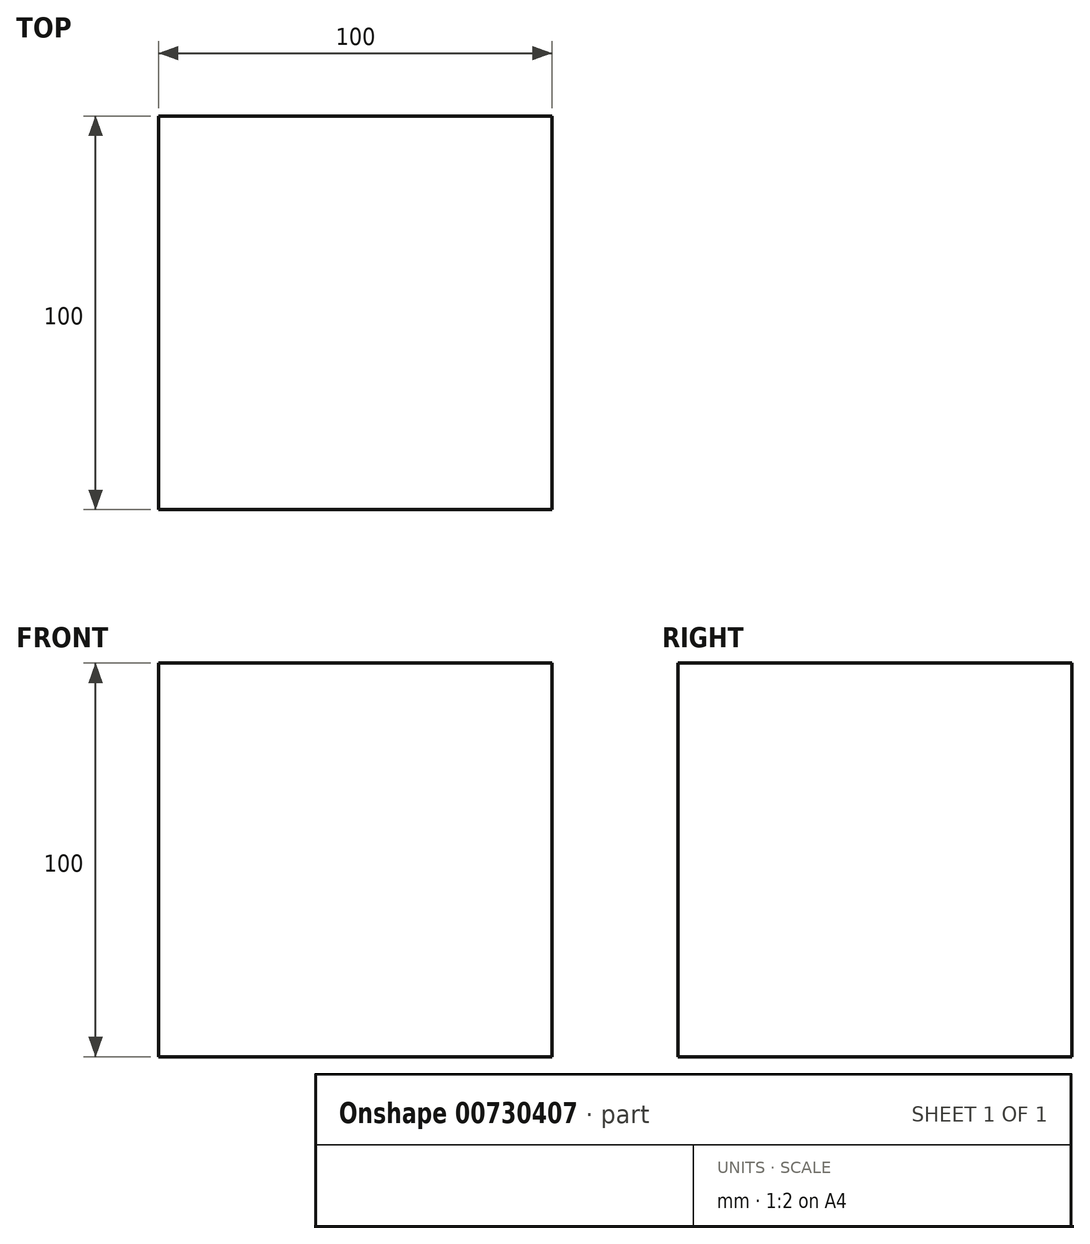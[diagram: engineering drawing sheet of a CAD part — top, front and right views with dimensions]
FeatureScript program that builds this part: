
annotation { "Feature Type Name" : "Feature", "Feature Type Description" : "" }
export const myFeature = defineFeature(function(context is Context, id is Id, definition is map)
    precondition{}
    {
        {
            var Q0;
            Q0=qCreatedBy(makeId("Front.planeOp"),FACE);
            var sketch = newSketch(context, id + "F0", { "sketchPlane" : qUnion([Q0])});
            skLineSegment(sketch, "E0.bottom", {"start": v(50, -50) * mm, "end": v(-50, -50) * mm});
            skLineSegment(sketch, "E0.top", {"start": v(50, 50) * mm, "end": v(-50, 50) * mm});
            skLineSegment(sketch, "E0.left", {"start": v(50, -50) * mm, "end": v(50, 50) * mm});
            skLineSegment(sketch, "E0.right", {"start": v(-50, -50) * mm, "end": v(-50, 50) * mm});
            skPoint(sketch, "E0.middle", {"position": v(0, 0) * mm});
            skSolve(sketch);
        }
        {
            var Q0;
            Q0=makeQuery(id+"F0.imprint","IMPRINT",FACE,{"disambiguationData":[TD([[makeQuery(id+"F0.imprint","IMPRINT",EDGE,{"derivedFrom":sQuery(id+"F0.wireOp",EDGE,"E0.bottom")}),-1.0]])]});
            extrude(context, id + "F1", {"entities" : qUnion([Q0]), "depth" : 100 * mm, "offsetDistance" : 25 * mm});
        }
    });
